# Revit family: HL_RU_Anti-flooding valve_HL712.2-A-171212
name_source: partatom
category: Příslušenství trubek
units: mm (PartAtom-declared; Revit-internal decimal feet)

## family parameters
Kóta kulaté spojky = Použít průměr
Nadpis OmniClass = Non-Return Valves for Liquid Services
Ořezat dutým tvarem při načtení = Ne
Sdílené = Ne
Typ dílu = Normální
Vždy vertikální = Ano
Založené na pracovní rovině = Ne
Číslo OmniClass = 23.65.55.14.21

## types (1)
- HL_Механический канализационный затвор_HL712.2
    Cena = 0 $
    EAN = 9003076971220
    Indexovaná poznámka = HL712.2
    Komentáře k typům = Механический канализационный затвор DN125 с 2 заслонками из нержавеющей стали и ручным затвором.
    Model = HL712.2
    Popis = Механический канализационный затвор
    URL = http://www.hutterer-lechner.com
    Výchozí výška = 0 mm  [stored 0 ft]
    Výrobce = HL Hutterer & Lechner GmbH
    ВЕС = 3,32 kg
    ВЫСОТА МОНТАЖА = 320 mm
    МАТЕРИАЛ = ABS
    НОМИНАЛЬНЫЙ ДИАМЕТР = 125 mm
    НОМИНАЛЬНЫЙ ДИАМЕТР 2 = 125 mm
    РАЗМЕР = DN125

note: [stored X ft] marks values corroborated as IEEE doubles in the binary element streams (Revit-internal decimal feet)
